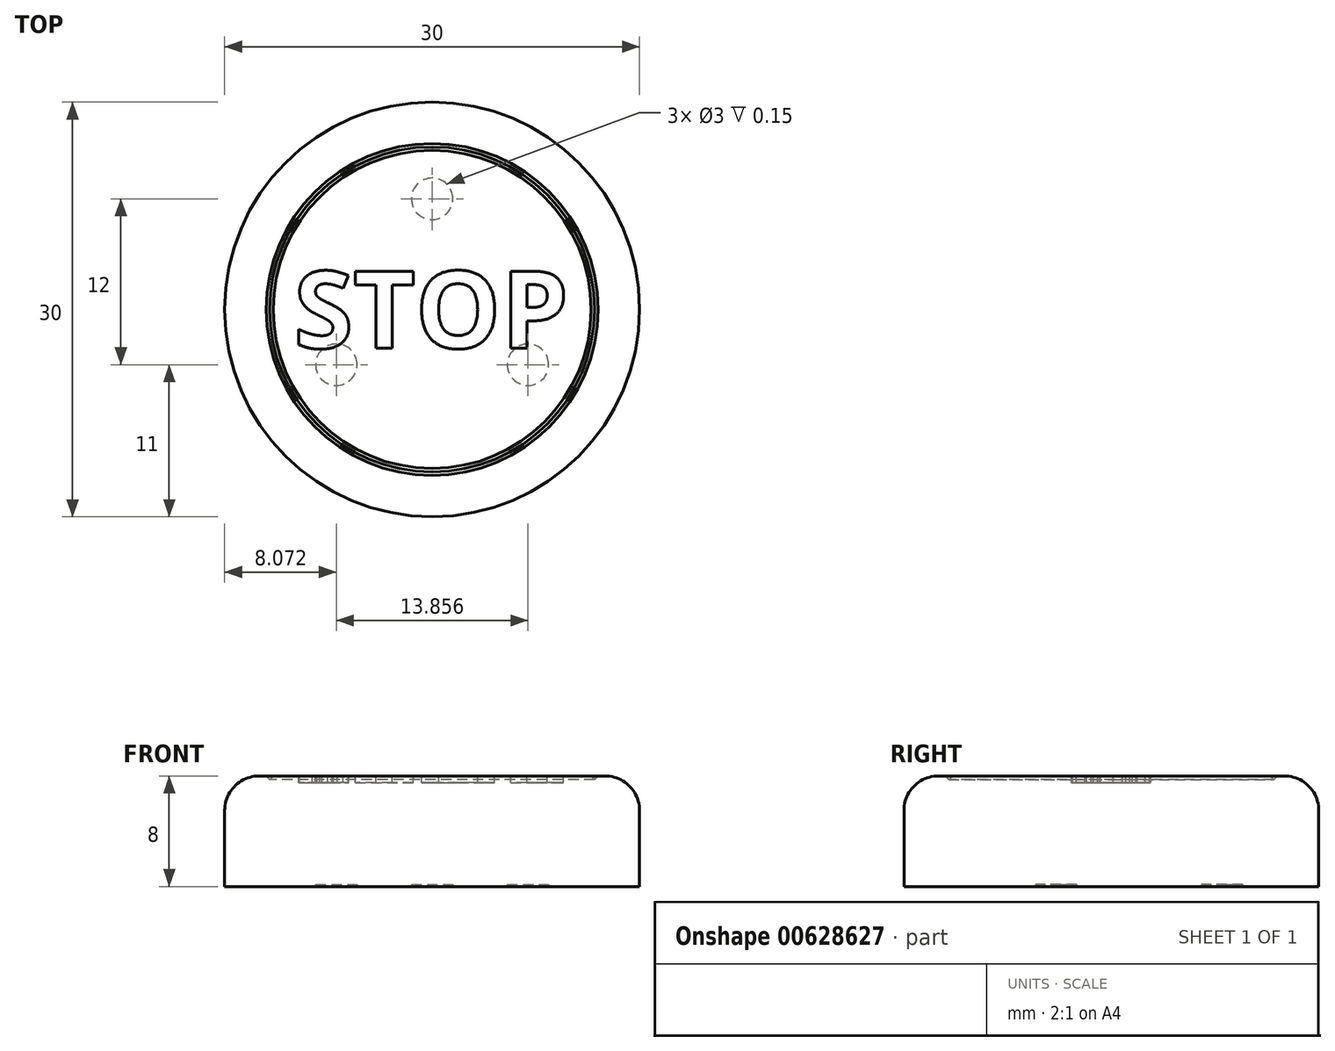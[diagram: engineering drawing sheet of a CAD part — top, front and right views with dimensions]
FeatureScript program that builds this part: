
annotation { "Feature Type Name" : "Feature", "Feature Type Description" : "" }
export const myFeature = defineFeature(function(context is Context, id is Id, definition is map)
    precondition{}
    {
        {
            var Q0;
            Q0=qCreatedBy(makeId("Top.planeOp"),FACE);
            var sketch = newSketch(context, id + "F0", { "sketchPlane" : qUnion([Q0])});
            skCircle(sketch, "E0", {"center": v(0, 0) * mm, "radius": 15 * mm});
            skSolve(sketch);
        }
        {
            var Q0;
            Q0=makeQuery(id+"F0.imprint","IMPRINT",FACE,{"disambiguationData":[TD([[makeQuery(id+"F0.imprint","IMPRINT",EDGE,{"derivedFrom":sQuery(id+"F0.wireOp",EDGE,"E0")}),1.0]])]});
            extrude(context, id + "F1", {"entities" : qUnion([Q0]), "depth" : 8 * mm, "offsetDistance" : 25 * mm});
        }
        {
            var Q0;
            Q0=makeQuery(id+"F1.opExtrude","CAP_FACE",FACE,{"disambiguationData":[OSD([sQuery(id+"F0.wireOp",EDGE,"E0")])],"isStart":false});
            var sketch = newSketch(context, id + "F2", { "sketchPlane" : qUnion([Q0])});
            skCircle(sketch, "E1", {"center": v(0, 0) * mm, "radius": 12 * mm});
            skCircle(sketch, "E2", {"center": v(0, 0) * mm, "radius": 11.5 * mm});
            skSolve(sketch);
        }
        {
            var Q0;
            Q0=makeQuery(id+"F2.imprint","IMPRINT",FACE,{"disambiguationData":[TD([[makeQuery(id+"F2.imprint","IMPRINT",EDGE,{"derivedFrom":sQuery(id+"F2.wireOp",EDGE,"E1")}),1.0]])]});
            extrude(context, id + "F3", {"entities" : qUnion([Q0]), "operationType" : NewBodyOperationType.REMOVE, "oppositeDirection" : true, "depth" : 0.5 * mm, "offsetDistance" : 25 * mm, "hasDraft" : true, "draftAngle" : 45 * degree, "draftPullDirection" : true});
        }
        {
            var Q0;
            Q0=makeQuery(id+"F1.opExtrude","CAP_EDGE",EDGE,{"disambiguationData":[OSD([sQuery(id+"F0.wireOp",EDGE,"E0")])],"isStart":false});
            fillet(context, id + "F4", {"entities" : qUnion([Q0]), "radius" : 2.5 * mm, "tangentPropagation" : true, "allowEdgeOverflow" : false});
        }
        {
            var Q0;
            Q0=makeQuery(id+"F3.boolean.opBoolean","SPLIT",FACE,{"disambiguationData":[TD([makeQuery(id+"F3.opExtrude","SWEPT_FACE",FACE,{"disambiguationData":[OSD([sQuery(id+"F2.wireOp",EDGE,"E2")])]})])],"derivedFrom":makeQuery(id+"F1.opExtrude","CAP_FACE",FACE,{"disambiguationData":[OSD([sQuery(id+"F0.wireOp",EDGE,"E0")])],"isStart":false})});
            var sketch = newSketch(context, id + "F5", { "sketchPlane" : qUnion([Q0])});
            skText(sketch, "E3", { "text": "STOP", "fontName": "OpenSans-Bold.ttf"});
            skLineSegment(sketch, "E4", {"start": v(-10, 0) * mm, "end": v(10, 0) * mm, "construction": true});
            const initialGuessF5  = {"E3": [-0.01, -0.0028, 1, 0, 0.0056]};
            skSetInitialGuess(sketch, initialGuessF5);
            skSolve(sketch);
        }
        {
            var Q0;
            Q0 = qSketchRegion(id + "F5", true);
            extrude(context, id + "F6", {"entities" : qUnion([Q0]), "operationType" : NewBodyOperationType.REMOVE, "oppositeDirection" : true, "depth" : 0.5 * mm, "offsetDistance" : 25 * mm});
        }
        {
            var Q0;
            Q0=makeQuery(id+"F1.opExtrude","CAP_FACE",FACE,{"disambiguationData":[OSD([sQuery(id+"F0.wireOp",EDGE,"E0")])],"isStart":true});
            var sketch = newSketch(context, id + "F7", { "sketchPlane" : qUnion([Q0])});
            skCircle(sketch, "E5", {"center": v(0, -8) * mm, "radius": 1.5 * mm});
            skCircle(sketch, "E6.1.0", {"center": v(6.93, 4) * mm, "radius": 1.5 * mm});
            skCircle(sketch, "E6.2.0", {"center": v(-6.93, 4) * mm, "radius": 1.5 * mm});
            skPoint(sketch, "E6.center", {"position": v(0, 0) * mm});
            skSolve(sketch);
        }
        {
            var Q0;
            Q0 = qSketchRegion(id + "F7", true);
            extrude(context, id + "F8", {"entities" : qUnion([Q0]), "operationType" : NewBodyOperationType.REMOVE, "oppositeDirection" : true, "depth" : 0.15 * mm, "offsetDistance" : 25 * mm});
        }
    });
